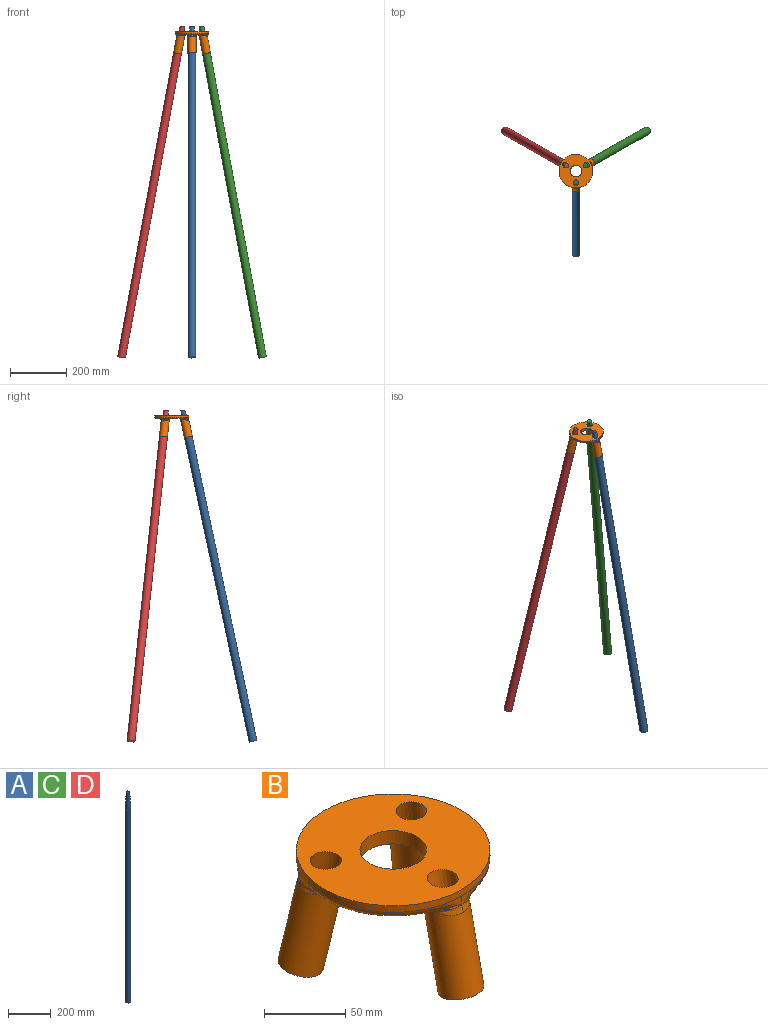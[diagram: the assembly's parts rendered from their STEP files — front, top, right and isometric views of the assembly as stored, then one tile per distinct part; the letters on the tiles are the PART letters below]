
ASSEMBLY  parts=4 mates=1
PART A: 4 faces, bbox 28x28x1200 mm
  f0: cylinder r=14mm len=1103.96mm, axis (0,0,1), area 97109.8mm2, adj f1,f2
  f1: plane 28x28mm, normal (0,0,-1), area 615.8mm2, adj f0
  f2: cone r=8mm half-angle=3.6deg, axis (0,0,-1), area 6650.5mm2, adj f0,f3
  f3: plane 16x16mm, normal (0,0,1), area 201.1mm2, adj f2
PART B: 196 faces, bbox 131.1x136.1x83.2 mm
  f0: plane 109.27x106.03mm, normal (0,0,-1), area 5313.4mm2, adj f10,f11,f13,f21,f22,f31,f33,f34
  f1: plane 120.13x120.13mm, normal (0,0,1), area 8996.4mm2, adj f2,f3,f14,f24,f33
  f2: cylinder r=59.64mm len=119.27mm, axis (0,0,1), area 1873.5mm2, adj f1,f5,f11,f12,f13,f16,f22,f23
  f3: cone r=9.93mm half-angle=3.6deg, axis (0,-0.21,-0.98), area 5751.4mm2, adj f1,f4
  f4: cylinder r=14.25mm len=70.44mm, axis (0,-0.21,-0.98), area 5509.6mm2, adj f3,f7,f8,f10
  f5: bspline ~20.25x6.11mm, area 100.3mm2, adj f2,f6,f11,f12
  f6: bspline ~19.33x8.91mm, area 63.8mm2, adj f5,f7,f10,f11
  f7: bspline ~14.95x10.97mm, area 72.3mm2, adj f4,f6,f8,f10
  f8: bspline ~14.95x10.97mm, area 72.3mm2, adj f4,f7,f9,f10
  f9: bspline ~19.33x8.91mm, area 63.8mm2, adj f8,f10,f12,f13
  f10: bspline ~38.5x25.47mm, area 447.9mm2, adj f0,f4,f6,f7,f8,f9
  f11: torus R=54.64mm, axis (0,0,1), area 641.9mm2, adj f0,f2,f5,f6,f20,f23
  f12: bspline ~20.25x6.11mm, area 100.3mm2, adj f2,f5,f9,f13
  f13: torus R=54.64mm, axis (0,0,1), area 641.9mm2, adj f0,f2,f9,f12,f26,f27
  f14: cone r=9.93mm half-angle=3.6deg, axis (-0.18,0.1,-0.98), area 5751.4mm2, adj f1,f15
  f15: cylinder r=14.25mm len=70.44mm, axis (-0.18,0.1,-0.98), area 5509.6mm2, adj f14,f18,f19,f21
  f16: bspline ~15.82x13.81mm, area 100.3mm2, adj f2,f17,f22,f23
  f17: bspline ~16.44x14.34mm, area 63.8mm2, adj f16,f18,f21,f22
  f18: bspline ~16.36x8.51mm, area 72.3mm2, adj f15,f17,f19,f21
  f19: bspline ~18.08x5.54mm, area 72.3mm2, adj f15,f18,f20,f21
  f20: bspline ~20.2x5.72mm, area 63.8mm2, adj f11,f19,f21,f23
  f21: bspline ~38.19x33.79mm, area 447.9mm2, adj f0,f15,f17,f18,f19,f20
  f22: torus R=54.64mm, axis (0,0,1), area 641.9mm2, adj f0,f2,f16,f17,f30,f32
  f23: bspline ~19.32x7.16mm, area 100.3mm2, adj f2,f11,f16,f20
  f24: cone r=9.93mm half-angle=3.6deg, axis (0.18,0.1,-0.98), area 5751.4mm2, adj f1,f25
  f25: cylinder r=14.25mm len=70.44mm, axis (0.18,0.1,-0.98), area 5509.6mm2, adj f24,f28,f29,f31
  f26: bspline ~19.32x7.16mm, area 100.3mm2, adj f2,f13,f27,f32
  f27: bspline ~20.2x5.72mm, area 63.8mm2, adj f13,f26,f28,f31
  f28: bspline ~18.08x5.54mm, area 72.3mm2, adj f25,f27,f29,f31
  f29: bspline ~16.36x8.51mm, area 72.3mm2, adj f25,f28,f30,f31
  f30: bspline ~16.44x14.34mm, area 63.8mm2, adj f22,f29,f31,f32
  f31: bspline ~38.19x33.79mm, area 447.9mm2, adj f0,f25,f27,f28,f29,f30
  f32: bspline ~15.82x13.81mm, area 100.3mm2, adj f2,f22,f26,f30
  f33: cylinder r=20.5mm len=41mm, axis (0,0,1), area 1288.1mm2, adj f0,f1
  f34: plane 2.56x1mm, normal (-1,0,0), area 2.6mm2, adj f0,f35,f50,f51
  f35: plane 1.18x1mm, normal (0,1,0), area 1.2mm2, adj f0,f34,f36,f51
  f36: plane 2.89x1mm, normal (1,0,0), area 2.9mm2, adj f0,f35,f37,f51
  f37: extruded ~1.3x1mm, area 1.4mm2, adj f0,f36,f38,f51
  f38: extruded ~1.11x1mm, area 1.2mm2, adj f0,f37,f39,f51
  f39: extruded ~1x0.87mm, area 0.9mm2, adj f0,f38,f40,f51
  f40: extruded ~1x0.75mm, area 1mm2, adj f0,f39,f41,f51
  f41: plane 1x0.02mm, normal (0,-1,0), area 0mm2, adj f0,f40,f42,f51
  f42: extruded ~1x0.91mm, area 0.9mm2, adj f0,f41,f43,f51
  f43: plane 1.13x1mm, normal (0,-1,0), area 1.1mm2, adj f0,f42,f44,f51
  f44: extruded ~1.02x1mm, area 1mm2, adj f0,f43,f45,f51
  f45: plane 3.54x1mm, normal (-1,0,0), area 3.5mm2, adj f0,f44,f46,f51
  f46: plane 1.18x1mm, normal (0,1,0), area 1.2mm2, adj f0,f45,f47,f51
  f47: plane 2.44x1mm, normal (1,0,0), area 2.4mm2, adj f0,f46,f48,f51
  f48: extruded ~1x0.95mm, area 1mm2, adj f0,f47,f49,f51
  f49: extruded ~1x0.69mm, area 0.8mm2, adj f0,f48,f50,f51
  f50: extruded ~1.2x1mm, area 1.6mm2, adj f0,f34,f49,f51
  f51: plane 4.64x4.17mm, normal (0,0,-1), area 12mm2, adj f34,f35,f36,f37,f38,f39,f40,f41
  f52: plane 3.49x1mm, normal (1,0,0), area 3.5mm2, adj f0,f53,f68,f69
  f53: plane 1.18x1mm, normal (0,-1,0), area 1.2mm2, adj f0,f52,f54,f69
  f54: plane 2.24x1mm, normal (-1,0,0), area 2.2mm2, adj f0,f53,f55,f69
  f55: extruded ~1.06x1mm, area 1.1mm2, adj f0,f54,f56,f69
  f56: extruded ~1x0.69mm, area 0.8mm2, adj f0,f55,f57,f69
  f57: extruded ~1x0.51mm, area 0.5mm2, adj f0,f56,f58,f69
  f58: plane 1x0.99mm, normal (-1,0,0), area 1mm2, adj f0,f57,f59,f69
  f59: extruded ~1x0.37mm, area 0.4mm2, adj f0,f58,f60,f69
  f60: extruded ~1x0.46mm, area 0.5mm2, adj f0,f59,f61,f69
  f61: extruded ~1x0.32mm, area 0.4mm2, adj f0,f60,f62,f69
  f62: extruded ~1x0.68mm, area 0.7mm2, adj f0,f61,f63,f69
  f63: plane 1x0.02mm, normal (0,1,0), area 0mm2, adj f0,f62,f64,f69
  f64: extruded ~1x0.51mm, area 0.5mm2, adj f0,f63,f65,f69
  f65: extruded ~1x0.46mm, area 0.5mm2, adj f0,f64,f66,f69
  f66: plane 1.13x1mm, normal (0,1,0), area 1.1mm2, adj f0,f65,f67,f69
  f67: extruded ~1x0.44mm, area 0.4mm2, adj f0,f66,f68,f69
  f68: extruded ~1x0.63mm, area 0.6mm2, adj f0,f52,f67,f69
  f69: plane 4.64x2.66mm, normal (0,0,-1), area 6.7mm2, adj f52,f53,f54,f55,f56,f57,f58,f59
  f70: extruded ~1.29x1mm, area 1.4mm2, adj f0,f71,f98,f99
  f71: extruded ~1x0.94mm, area 1mm2, adj f0,f70,f72,f99
  f72: extruded ~1.05x1mm, area 1.2mm2, adj f0,f71,f73,f99
  f73: plane 1x0.02mm, normal (-1,0,0), area 0mm2, adj f0,f72,f74,f99
  f74: extruded ~1x0.94mm, area 1.1mm2, adj f0,f73,f75,f99
  f75: extruded ~1x0.91mm, area 1mm2, adj f0,f74,f76,f99
  f76: extruded ~1.16x1mm, area 1.3mm2, adj f0,f75,f77,f99
  f77: extruded ~1.46x1mm, area 1.5mm2, adj f0,f76,f78,f99
  f78: extruded ~1.42x1mm, area 1.5mm2, adj f0,f77,f79,f99
  f79: extruded ~1.2x1mm, area 1.4mm2, adj f0,f78,f80,f99
  f80: plane 1.18x1mm, normal (0.07,-1,0), area 1.2mm2, adj f0,f79,f81,f99
  f81: extruded ~1x0.57mm, area 0.6mm2, adj f0,f80,f82,f99
  f82: extruded ~1x0.59mm, area 0.6mm2, adj f0,f81,f83,f99
  f83: extruded ~1x0.6mm, area 0.6mm2, adj f0,f82,f84,f99
  f84: extruded ~1x0.57mm, area 0.6mm2, adj f0,f83,f85,f99
  f85: extruded ~1x0.6mm, area 0.7mm2, adj f0,f84,f86,f99
  f86: extruded ~1x0.77mm, area 0.8mm2, adj f0,f85,f87,f99
  f87: plane 1x0.39mm, normal (0,1,0), area 0.4mm2, adj f0,f86,f88,f99
  f88: plane 1x0.96mm, normal (1,0,0), area 1mm2, adj f0,f87,f89,f99
  f89: plane 1x0.41mm, normal (0,-1,0), area 0.4mm2, adj f0,f88,f90,f99
  f90: extruded ~1x0.85mm, area 0.9mm2, adj f0,f89,f91,f99
  f91: extruded ~1x0.61mm, area 0.7mm2, adj f0,f90,f92,f99
  f92: extruded ~1x0.64mm, area 0.7mm2, adj f0,f91,f93,f99
  f93: extruded ~1x0.66mm, area 0.7mm2, adj f0,f92,f94,f99
  f94: extruded ~1x0.97mm, area 1.4mm2, adj f0,f93,f95,f99
  f95: plane 1.2x1mm, normal (0.09,1,0), area 1.2mm2, adj f0,f94,f96,f99
  f96: extruded ~1.27x1mm, area 1.5mm2, adj f0,f95,f97,f99
  f97: extruded ~1.52x1mm, area 1.6mm2, adj f0,f96,f98,f99
  f98: extruded ~1.56x1mm, area 1.7mm2, adj f0,f70,f97,f99
  f99: plane 6.12x4.29mm, normal (0,0,-1), area 13.6mm2, adj f70,f71,f72,f73,f74,f75,f76,f77
  f100: extruded ~1x0.65mm, area 0.7mm2, adj f101,f157,f158,f193
  f101: extruded ~1x0.68mm, area 0.7mm2, adj f100,f102,f158,f193
  f102: extruded ~1x0.76mm, area 0.8mm2, adj f101,f103,f158,f193
  f103: extruded ~1x0.51mm, area 0.7mm2, adj f102,f104,f158,f193
  f104: extruded ~1x0.54mm, area 0.6mm2, adj f103,f105,f158,f193
  f105: extruded ~1x0.62mm, area 0.7mm2, adj f104,f106,f158,f193
  f106: extruded ~1x0.76mm, area 0.8mm2, adj f105,f107,f158,f193
  f107: extruded ~1x0.99mm, area 1mm2, adj f106,f108,f158,f193
  f108: extruded ~1x0.75mm, area 0.9mm2, adj f107,f109,f158,f193
  f109: extruded ~1x0.71mm, area 0.8mm2, adj f108,f157,f158,f193
  f110: extruded ~1.4x1mm, area 1.4mm2, adj f0,f111,f156,f158
  f111: extruded ~1.61x1mm, area 1.7mm2, adj f0,f110,f112,f158
  f112: extruded ~1.14x1.08mm, area 1.6mm2, adj f0,f111,f113,f158
  f113: extruded ~1.77x1mm, area 1.8mm2, adj f0,f112,f114,f158
  f114: extruded ~2.1x1mm, area 2.2mm2, adj f0,f113,f115,f158
  f115: extruded ~1.5x1.47mm, area 2.1mm2, adj f0,f114,f116,f158
  f116: extruded ~2.16x1mm, area 2.2mm2, adj f0,f115,f117,f158
  f117: extruded ~1.74x1mm, area 1.8mm2, adj f0,f116,f118,f158
  f118: extruded ~1.18x1.16mm, area 1.7mm2, adj f0,f117,f119,f158
  f119: extruded ~1.75x1mm, area 1.8mm2, adj f0,f118,f120,f158
  f120: extruded ~1.39x1mm, area 1.4mm2, adj f0,f119,f121,f158
  f121: extruded ~1.38x1mm, area 1.5mm2, adj f0,f120,f122,f158
  f122: plane 1x0.51mm, normal (-0.89,0.45,0), area 0.6mm2, adj f0,f121,f123,f158
  f123: extruded ~2.48x1mm, area 2.6mm2, adj f0,f122,f124,f158
  f124: extruded ~1.42x1mm, area 1.5mm2, adj f0,f123,f125,f158
  f125: extruded ~1x0.94mm, area 1.4mm2, adj f0,f124,f126,f158
  f126: extruded ~1.44x1mm, area 1.5mm2, adj f0,f125,f127,f158
  f127: extruded ~1.87x1mm, area 1.9mm2, adj f0,f126,f128,f158
  f128: extruded ~1.28x1.21mm, area 1.8mm2, adj f0,f127,f129,f158
  f129: extruded ~1.78x1mm, area 1.9mm2, adj f0,f128,f130,f158
  f130: extruded ~1.41x1mm, area 1.5mm2, adj f0,f129,f131,f158
  f131: extruded ~1x0.93mm, area 1.3mm2, adj f0,f130,f132,f158
  f132: extruded ~1.3x1mm, area 1.4mm2, adj f0,f131,f133,f158
  f133: extruded ~1.08x1mm, area 1.1mm2, adj f0,f132,f134,f158
  f134: extruded ~1x0.78mm, area 0.9mm2, adj f0,f133,f135,f158
  f135: extruded ~1x0.64mm, area 0.7mm2, adj f0,f134,f136,f158
  f136: extruded ~1x0.23mm, area 0.3mm2, adj f0,f135,f137,f158
  f137: extruded ~1x0.3mm, area 0.3mm2, adj f0,f136,f138,f158
  f138: extruded ~1.01x1mm, area 1mm2, adj f0,f137,f139,f158
  f139: plane 2.13x1mm, normal (-0.97,-0.22,0), area 2.2mm2, adj f0,f138,f140,f158
  f140: plane 1x0.66mm, normal (0,1,0), area 0.7mm2, adj f0,f139,f141,f158
  f141: plane 1x0.64mm, normal (0.97,0.25,0), area 0.7mm2, adj f0,f140,f142,f158
  f142: plane 1x0.03mm, normal (0,1,0), area 0mm2, adj f0,f141,f143,f158
  f143: extruded ~1.11x1mm, area 1.4mm2, adj f0,f142,f144,f158
  f144: extruded ~1.08x1mm, area 1.2mm2, adj f0,f143,f145,f158
  f145: extruded ~1x0.95mm, area 1.2mm2, adj f0,f144,f146,f158
  f146: extruded ~1.29x1mm, area 1.3mm2, adj f0,f145,f147,f158
  f147: extruded ~1.19x1mm, area 1.3mm2, adj f0,f146,f148,f158
  f148: extruded ~1.03x1mm, area 1.1mm2, adj f0,f147,f149,f158
  f149: extruded ~1x0.85mm, area 0.9mm2, adj f0,f148,f150,f158
  f150: extruded ~1x0.72mm, area 1mm2, adj f0,f149,f151,f158
  f151: plane 1x0.03mm, normal (0,-1,0), area 0mm2, adj f0,f150,f152,f158
  f152: extruded ~1x0.28mm, area 0.3mm2, adj f0,f151,f153,f158
  f153: extruded ~1x0.53mm, area 0.6mm2, adj f0,f152,f154,f158
  f154: extruded ~1x0.6mm, area 0.6mm2, adj f0,f153,f155,f158
  f155: extruded ~1.02x1mm, area 1.1mm2, adj f0,f154,f156,f158
  f156: extruded ~1x0.99mm, area 1.2mm2, adj f0,f110,f155,f158
  f157: extruded ~1x0.65mm, area 0.7mm2, adj f100,f109,f158,f193
  f158: plane 7.49x7.42mm, normal (0,0,-1), area 21.3mm2, adj f100,f101,f102,f103,f104,f105,f106,f107
  f159: extruded ~1.51x1mm, area 1.6mm2, adj f160,f175,f176,f194
  f160: extruded ~1.55x1mm, area 1.7mm2, adj f159,f161,f176,f194
  f161: extruded ~1.29x1mm, area 1.4mm2, adj f160,f162,f176,f194
  f162: extruded ~1.27x1mm, area 1.4mm2, adj f161,f163,f176,f194
  f163: extruded ~1.54x1mm, area 1.6mm2, adj f162,f164,f176,f194
  f164: extruded ~1.51x1mm, area 1.6mm2, adj f163,f165,f176,f194
  f165: extruded ~1.29x1mm, area 1.4mm2, adj f164,f175,f176,f194
  f166: extruded ~1.63x1mm, area 1.7mm2, adj f0,f167,f174,f176
  f167: extruded ~2.22x1mm, area 2.4mm2, adj f0,f166,f168,f176
  f168: extruded ~2.2x1mm, area 2.4mm2, adj f0,f167,f169,f176
  f169: extruded ~2.2x1mm, area 2.4mm2, adj f0,f168,f170,f176
  f170: extruded ~2.23x1mm, area 2.4mm2, adj f0,f169,f171,f176
  f171: extruded ~2.26x1mm, area 2.5mm2, adj f0,f170,f172,f176
  f172: extruded ~2.19x1mm, area 2.4mm2, adj f0,f171,f173,f176
  f173: extruded ~1.59x1mm, area 1.7mm2, adj f0,f172,f174,f176
  f174: extruded ~1.08x1.05mm, area 1.5mm2, adj f0,f166,f173,f176
  f175: extruded ~1.28x1mm, area 1.4mm2, adj f159,f165,f176,f194
  f176: plane 6.11x5.99mm, normal (0,0,-1), area 18mm2, adj f159,f160,f161,f162,f163,f164,f165,f166
  f177: extruded ~1.46x1mm, area 1.6mm2, adj f178,f191,f192,f195
  f178: extruded ~1.5x1mm, area 1.6mm2, adj f177,f179,f192,f195
  f179: extruded ~1.27x1mm, area 1.4mm2, adj f178,f180,f192,f195
  f180: plane 1.05x1mm, normal (0,1,0), area 1.1mm2, adj f179,f181,f192,f195
  f181: plane 4.01x1mm, normal (-1,0,0), area 4mm2, adj f180,f182,f192,f195
  f182: plane 1x0.88mm, normal (0,-1,0), area 0.9mm2, adj f181,f191,f192,f195
  f183: extruded ~1.6x1mm, area 1.7mm2, adj f0,f184,f190,f192
  f184: extruded ~2.17x1mm, area 2.4mm2, adj f0,f183,f185,f192
  f185: extruded ~2.32x1mm, area 2.5mm2, adj f0,f184,f186,f192
  f186: plane 2.15x1mm, normal (0,1,0), area 2.1mm2, adj f0,f185,f187,f192
  f187: plane 5.93x1mm, normal (1,0,0), area 5.9mm2, adj f0,f186,f188,f192
  f188: plane 2.4x1mm, normal (0,-1,0), area 2.4mm2, adj f0,f187,f189,f192
  f189: extruded ~1.51x1mm, area 1.6mm2, adj f0,f188,f190,f192
  f190: extruded ~1.05x1.02mm, area 1.5mm2, adj f0,f183,f189,f192
  f191: extruded ~1.42x1mm, area 1.5mm2, adj f177,f182,f192,f195
  f192: plane 5.93x5.29mm, normal (0,0,-1), area 18.2mm2, adj f177,f178,f179,f180,f181,f182,f183,f184
  f193: plane 3.04x2.27mm, normal (0,0,-1), area 5.3mm2, adj f100,f101,f102,f103,f104,f105,f106,f107
  f194: plane 4.15x3.47mm, normal (0,0,-1), area 11.8mm2, adj f159,f160,f161,f162,f163,f164,f165,f175
  f195: plane 4.01x2.8mm, normal (0,0,-1), area 9.9mm2, adj f177,f178,f179,f180,f181,f182,f191
PART C: same geometry as A
PART D: same geometry as A
PLACE A rot(axis=(-1,0,0),12deg) t=(0,-39.03,18.43)mm
PLACE B t=(0,0,-10)mm
PLACE C rot(axis=(-0.06,-0.1,0.99),120.4deg) t=(33.8,19.51,18.43)mm
PLACE D rot(axis=(-0.06,0.1,-0.99),120.4deg) t=(-33.8,19.51,18.43)mm
MATE fastened B.f3 <-> A.f2  axis (0,-0.21,-0.98) through (0,-58.99,-75.51)mm
